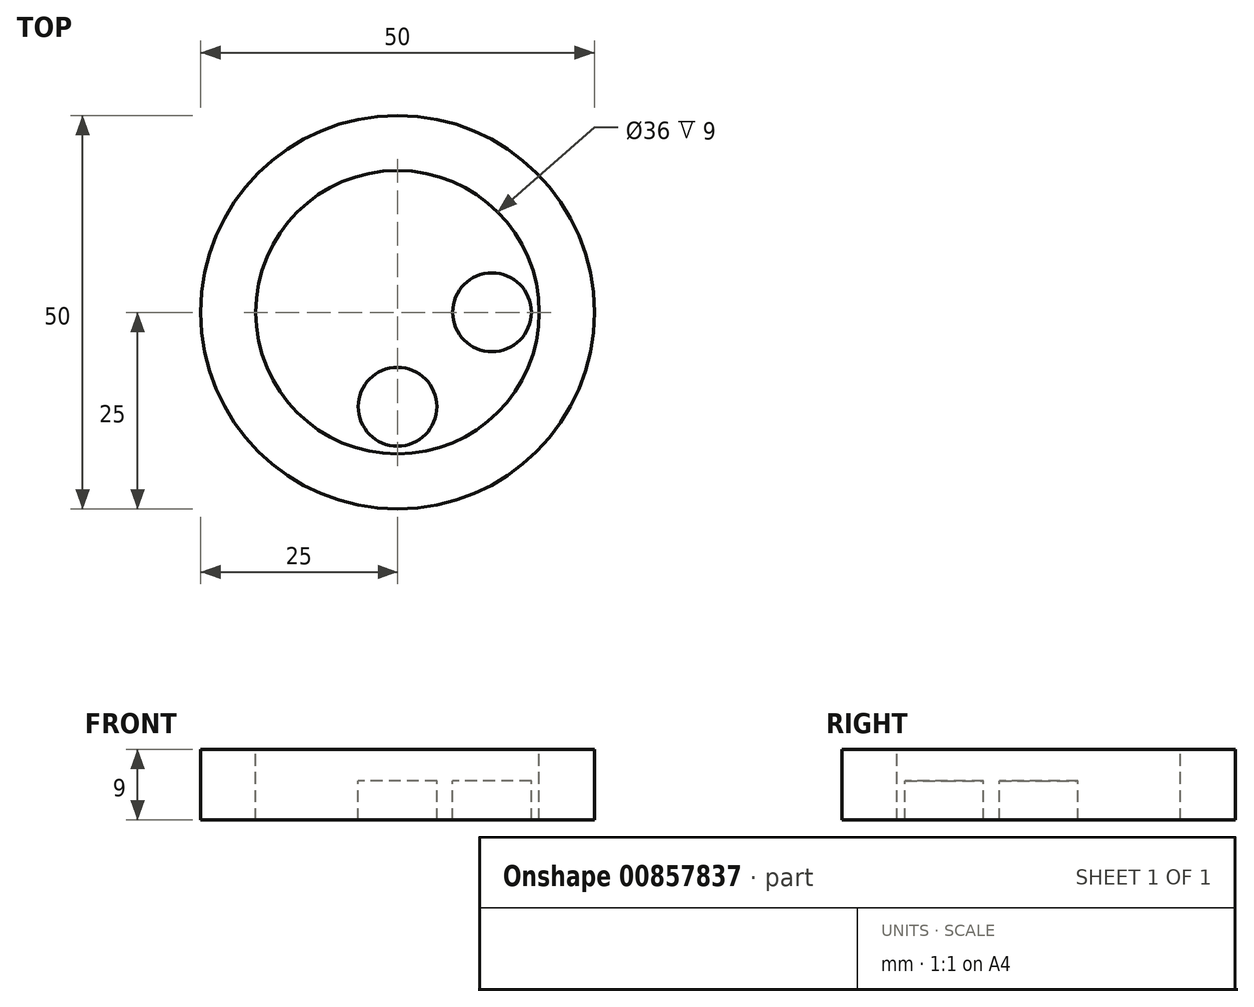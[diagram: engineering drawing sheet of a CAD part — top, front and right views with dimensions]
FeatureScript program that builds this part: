
annotation { "Feature Type Name" : "Feature", "Feature Type Description" : "" }
export const myFeature = defineFeature(function(context is Context, id is Id, definition is map)
    precondition{}
    {
        {
            var Q0;
            Q0=qCreatedBy(makeId("Front.planeOp"),FACE);
            var sketch = newSketch(context, id + "F0", { "sketchPlane" : qUnion([Q0])});
            skLineSegment(sketch, "E0", {"start": v(-4, -3.05) * mm, "end": v(-6, -3.05) * mm});
            skLineSegment(sketch, "E1", {"start": v(-6, -3.05) * mm, "end": v(-6, -2.05) * mm});
            skLineSegment(sketch, "E2", {"start": v(-6, -2.05) * mm, "end": v(-25, -2.05) * mm});
            skLineSegment(sketch, "E3", {"start": v(-25, -2.05) * mm, "end": v(-25, 6.95) * mm});
            skLineSegment(sketch, "E4", {"start": v(-25, 6.95) * mm, "end": v(-18, 6.95) * mm});
            skLineSegment(sketch, "E5", {"start": v(-18, 6.95) * mm, "end": v(-18, 2.95) * mm});
            skLineSegment(sketch, "E6", {"start": v(-18, 2.95) * mm, "end": v(-4, 2.95) * mm});
            skLineSegment(sketch, "E7", {"start": v(-4, 2.95) * mm, "end": v(-4, -3.05) * mm});
            skLineSegment(sketch, "E8", {"start": v(0, 13.68) * mm, "end": v(0, -7.94) * mm, "construction": true});
            skSolve(sketch);
        }
        {
            var Q0;
            Q0=makeQuery(id+"F0.imprint","IMPRINT",FACE,{"disambiguationData":[TD([[makeQuery(id+"F0.imprint","IMPRINT",EDGE,{"derivedFrom":sQuery(id+"F0.wireOp",EDGE,"E0")}),-1.0]])]});
            var Q1;
            Q1=sQuery(id+"F0.wireOp",EDGE,"E8");
            revolve(context, id + "F1", {"surfaceOperationType" : NewSurfaceOperationType.NEW, "entities" : qUnion([Q0]), "axis" : qUnion([Q1]), "revolveType" : RevolveType.FULL});
        }
        {
            var Q0;
            Q0=makeQuery(id+"F1.opRevolve","SWEPT_FACE",FACE,{"disambiguationData":[OSD([sQuery(id+"F0.wireOp",EDGE,"E6")])]});
            var sketch = newSketch(context, id + "F2", { "sketchPlane" : qUnion([Q0])});
            skCircle(sketch, "E9", {"center": v(0, 0) * mm, "radius": 12 * mm, "construction": true});
            skCircle(sketch, "E10", {"center": v(0, 12) * mm, "radius": 5 * mm});
            skCircle(sketch, "E11.MirrorC", {"center": v(0, -12) * mm, "radius": 5 * mm});
            skCircle(sketch, "E12", {"center": v(-12, 0) * mm, "radius": 5 * mm});
            skCircle(sketch, "E13.MirrorC", {"center": v(12, 0) * mm, "radius": 5 * mm});
            skSolve(sketch);
        }
        {
            var Q0;
            Q0=makeQuery(id+"F2.imprint","IMPRINT",FACE,{"disambiguationData":[TD([[makeQuery(id+"F2.imprint","IMPRINT",EDGE,{"derivedFrom":sQuery(id+"F2.wireOp",EDGE,"E12")}),1.0]])]});
            var Q1;
            Q1=makeQuery(id+"F2.imprint","IMPRINT",FACE,{"disambiguationData":[TD([[makeQuery(id+"F2.imprint","IMPRINT",EDGE,{"derivedFrom":sQuery(id+"F2.wireOp",EDGE,"E10")}),1.0]])]});
            var Q2;
            Q2=makeQuery(id+"F2.imprint","IMPRINT",FACE,{"disambiguationData":[TD([[makeQuery(id+"F2.imprint","IMPRINT",EDGE,{"derivedFrom":sQuery(id+"F2.wireOp",EDGE,"E13.MirrorC")}),-1.0]])]});
            var Q3;
            Q3=makeQuery(id+"F2.imprint","IMPRINT",FACE,{"disambiguationData":[TD([[makeQuery(id+"F2.imprint","IMPRINT",EDGE,{"derivedFrom":sQuery(id+"F2.wireOp",EDGE,"E11.MirrorC")}),-1.0]])]});
            extrude(context, id + "F3", {"entities" : qUnion([Q0, Q1, Q2, Q3]), "operationType" : NewBodyOperationType.REMOVE, "endBound" : BoundingType.THROUGH_ALL, "oppositeDirection" : true, "depth" : 25 * mm, "offsetDistance" : 25 * mm});
        }
    });
